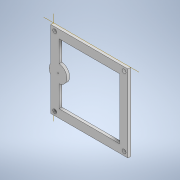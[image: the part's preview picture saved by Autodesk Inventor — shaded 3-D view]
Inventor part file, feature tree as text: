
AUTODESK INVENTOR PART (.ipt)
format: ipt  version: 2022 (Build 260153000, 153)  size: 201,728 bytes
history: native  units: mm
features: extrude x1, sketch x1
ambient origin geometry x8: Origin, YZ Plane, XZ Plane, XY Plane, X Axis, Y Axis, Z Axis, Center Point
bodies: Body1 (feature_tree)
feature tree (2):
  extrude  "Extrusión2"  Depth=5.0mm
  sketch  "Boceto1"  dims[d10=316.050854mm d11=295.117667mm d12=2.0mm d13=5.0mm d14=0.0mm]
